# Revit family: XOCT-XOCTXBC4
name_source: partatom
category: Furniture
units: mm (PartAtom-declared; Revit-internal decimal feet)

## family parameters
Always vertical = Yes
Cut with Voids When Loaded = No
OmniClass Number = 23.40.20.00
OmniClass Title = General Furniture and Specialties
Room Calculation Point = No
Shared = No
Work Plane-Based = No

## types (2) — shared parameters
Description = The airy structure of the Sierra tables blend perfectly into natural and urban settings.  The bent pipe structure with a diameter of 18mm is made of stainless steel or polyester powder coated steel tube and hot-dip galvanized steel.  Ready-equipped for fastening to the ground with bolts or joined together using steel plates.
Manufacturer = Via Seating
URL = https://viaseating.com
XOCT = Yes

## per-type parameters (varying)
| type | XOCT-XBC4 |
| XOCT | No |
| XOCT-XBC4 | Yes |

note: column(s) folded — value = type name in every type: Model

## geometry (parser evidence)
native form markers: Sweep x2
no freeform markers — native parametric forms only
